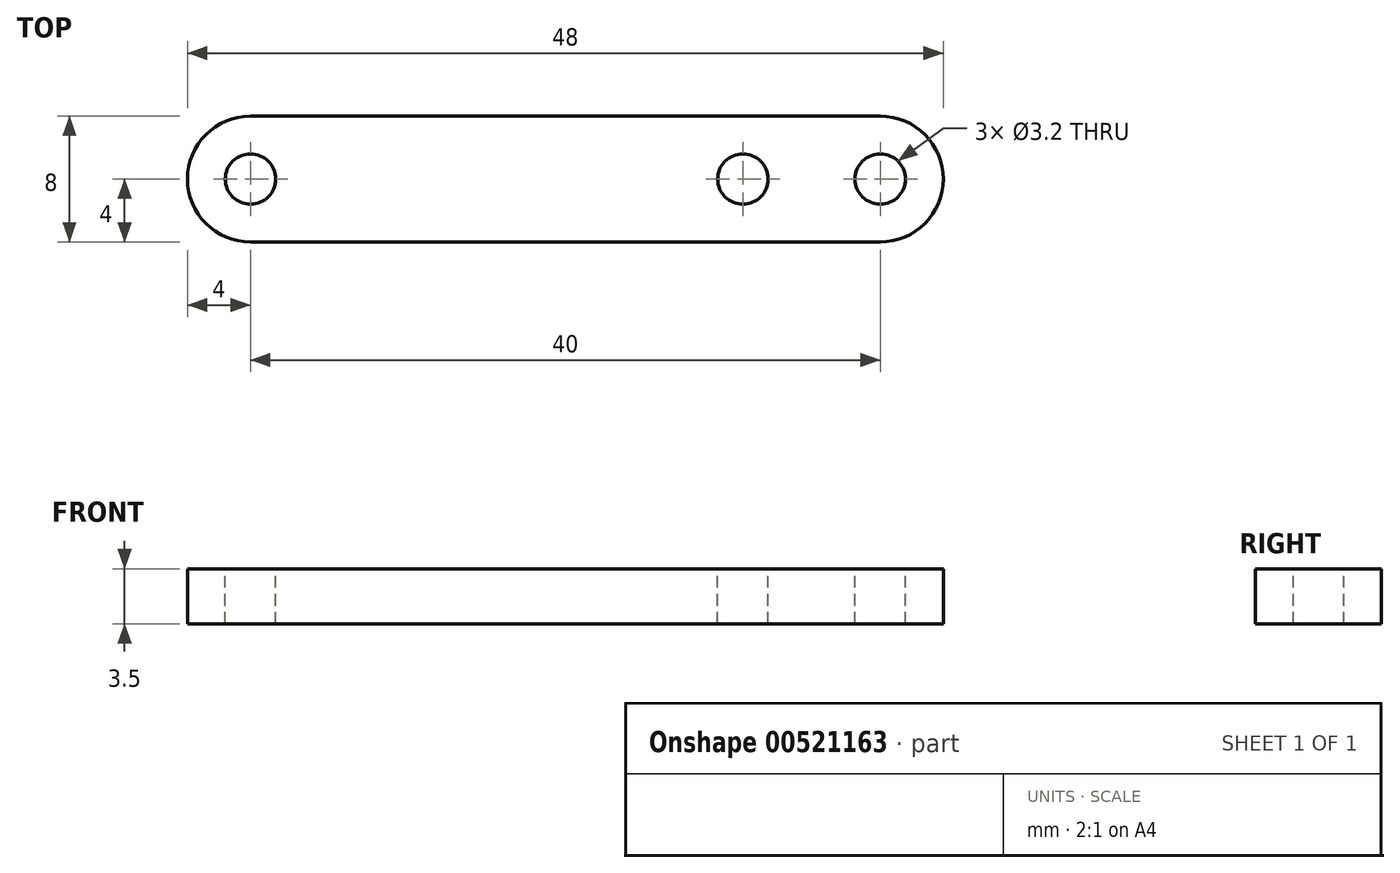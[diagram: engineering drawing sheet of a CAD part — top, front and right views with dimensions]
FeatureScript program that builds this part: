
annotation { "Feature Type Name" : "Feature", "Feature Type Description" : "" }
export const myFeature = defineFeature(function(context is Context, id is Id, definition is map)
    precondition{}
    {
        {
            var Q0;
            Q0=qCreatedBy(makeId("Top.planeOp"),FACE);
            var sketch = newSketch(context, id + "F0", { "sketchPlane" : qUnion([Q0])});
            skLineSegment(sketch, "E0.bottom", {"start": v(20, -4) * mm, "end": v(-20, -4) * mm});
            skLineSegment(sketch, "E0.top", {"start": v(20, 4) * mm, "end": v(-20, 4) * mm});
            skLineSegment(sketch, "E0.left", {"start": v(20, -4) * mm, "end": v(20, 4) * mm});
            skLineSegment(sketch, "E0.right", {"start": v(-20, -4) * mm, "end": v(-20, 4) * mm});
            skPoint(sketch, "E0.middle", {"position": v(0, 0) * mm});
            skCircle(sketch, "E1", {"center": v(-20, 0) * mm, "radius": 4 * mm});
            skCircle(sketch, "E2", {"center": v(20, 0) * mm, "radius": 4 * mm});
            skSolve(sketch);
        }
        {
            var Q0;
            Q0 = qSketchRegion(id + "F0", true);
            extrude(context, id + "F1", {"entities" : qUnion([Q0]), "depth" : 3.5 * mm, "offsetDistance" : 25 * mm});
        }
        {
            var Q0;
            Q0=makeQuery(id+"F1.opExtrude","CAP_FACE",FACE,{"disambiguationData":[OSD([sQuery(id+"F0.wireOp",EDGE,"E0.bottom"),sQuery(id+"F0.wireOp",EDGE,"E0.top"),sQuery(id+"F0.wireOp",EDGE,"E1"),sQuery(id+"F0.wireOp",EDGE,"E2")])],"isStart":false});
            var sketch = newSketch(context, id + "F2", { "sketchPlane" : qUnion([Q0])});
            skLineSegment(sketch, "E3.bottom", {"start": v(20, -4) * mm, "end": v(-20, -4) * mm});
            skLineSegment(sketch, "E3.top", {"start": v(20, 4) * mm, "end": v(-20, 4) * mm});
            skLineSegment(sketch, "E3.left", {"start": v(20, -4) * mm, "end": v(20, 4) * mm});
            skLineSegment(sketch, "E3.right", {"start": v(-20, -4) * mm, "end": v(-20, 4) * mm});
            skPoint(sketch, "E3.middle", {"position": v(0, 0) * mm});
            skCircle(sketch, "E4", {"center": v(-20, 0) * mm, "radius": 1.6 * mm});
            skCircle(sketch, "E5", {"center": v(20, 0) * mm, "radius": 1.6 * mm});
            skCircle(sketch, "E6", {"center": v(11.28, 0) * mm, "radius": 1.6 * mm});
            skSolve(sketch);
        }
        {
            var Q0;
            {var subQ0=sQuery(id+"F2.wireOp",EDGE,"E4");var subQ1=sQuery(id+"F2.wireOp",EDGE,"E3.right");var subQ2=makeQuery(id+"F2.imprint","INTERSECT",VERTEX,{"disambiguationData":[OD(0.0)],"derivedFrom":[subQ1,subQ0]});Q0=makeQuery(id+"F2.imprint","IMPRINT",FACE,{"disambiguationData":[TD([[makeQuery(id+"F2.imprint","IMPRINT",EDGE,{"disambiguationData":[TD([[subQ2,-1.0]])],"derivedFrom":subQ1}),1.0]])]});}
            var Q1;
            {var subQ0=sQuery(id+"F2.wireOp",EDGE,"E4");var subQ1=sQuery(id+"F2.wireOp",EDGE,"E3.right");var subQ2=makeQuery(id+"F2.imprint","INTERSECT",VERTEX,{"disambiguationData":[OD(0.0)],"derivedFrom":[subQ1,subQ0]});Q1=makeQuery(id+"F2.imprint","IMPRINT",FACE,{"disambiguationData":[TD([[makeQuery(id+"F2.imprint","IMPRINT",EDGE,{"disambiguationData":[TD([[subQ2,-1.0]])],"derivedFrom":subQ1}),-1.0]])]});}
            var Q2;
            {var subQ0=sQuery(id+"F2.wireOp",EDGE,"E5");var subQ1=sQuery(id+"F2.wireOp",EDGE,"E3.left");var subQ2=makeQuery(id+"F2.imprint","INTERSECT",VERTEX,{"disambiguationData":[OD(0.0)],"derivedFrom":[subQ1,subQ0]});Q2=makeQuery(id+"F2.imprint","IMPRINT",FACE,{"disambiguationData":[TD([[makeQuery(id+"F2.imprint","IMPRINT",EDGE,{"disambiguationData":[TD([[subQ2,-1.0]])],"derivedFrom":subQ1}),1.0]])]});}
            var Q3;
            {var subQ0=sQuery(id+"F2.wireOp",EDGE,"E5");var subQ1=sQuery(id+"F2.wireOp",EDGE,"E3.left");var subQ2=makeQuery(id+"F2.imprint","INTERSECT",VERTEX,{"disambiguationData":[OD(0.0)],"derivedFrom":[subQ1,subQ0]});Q3=makeQuery(id+"F2.imprint","IMPRINT",FACE,{"disambiguationData":[TD([[makeQuery(id+"F2.imprint","IMPRINT",EDGE,{"disambiguationData":[TD([[subQ2,-1.0]])],"derivedFrom":subQ1}),-1.0]])]});}
            var Q4;
            Q4=makeQuery(id+"F2.imprint","IMPRINT",FACE,{"disambiguationData":[TD([[makeQuery(id+"F2.imprint","IMPRINT",EDGE,{"derivedFrom":sQuery(id+"F2.wireOp",EDGE,"E6")}),1.0]])]});
            extrude(context, id + "F3", {"entities" : qUnion([Q0, Q1, Q2, Q3, Q4]), "operationType" : NewBodyOperationType.REMOVE, "endBound" : BoundingType.THROUGH_ALL, "oppositeDirection" : true, "depth" : 25 * mm, "offsetDistance" : 25 * mm});
        }
    });
